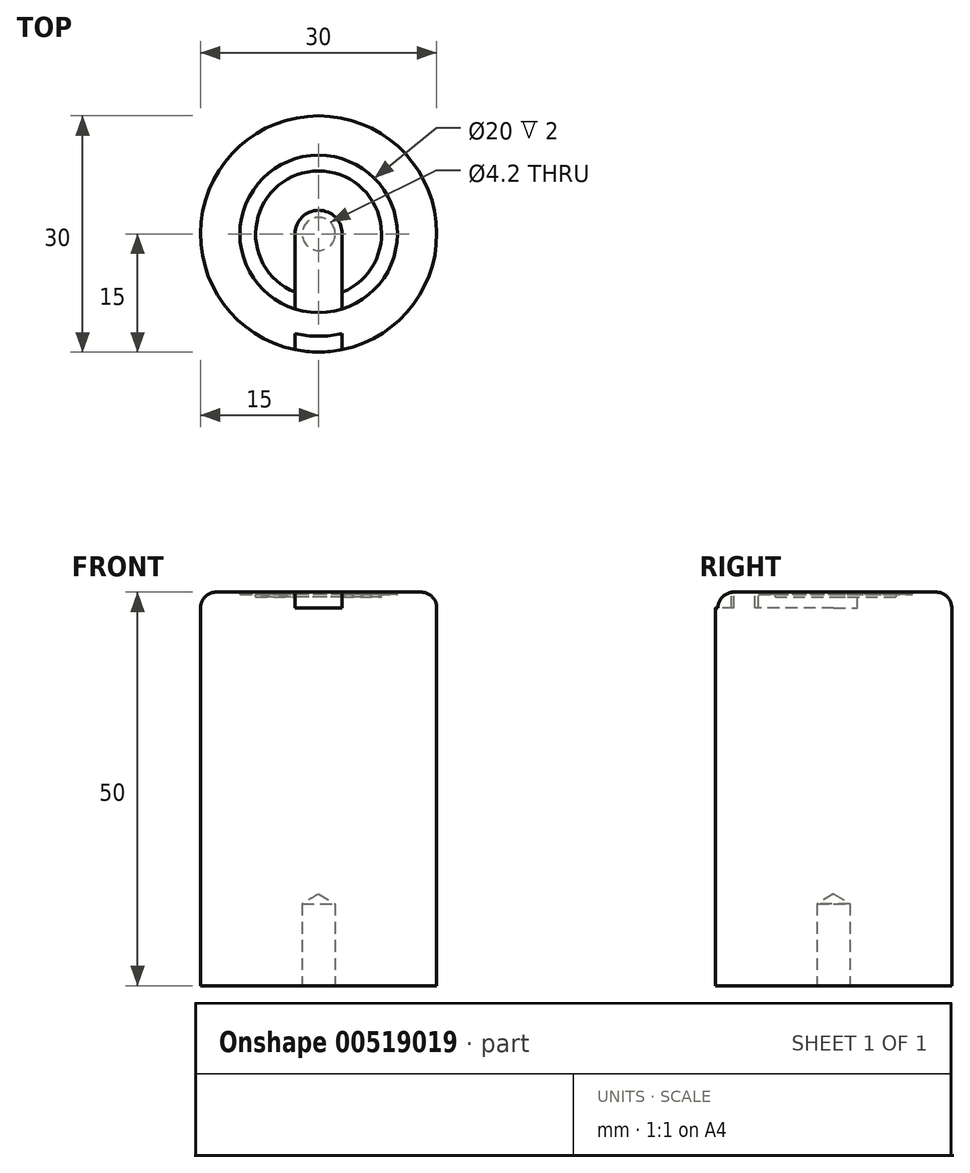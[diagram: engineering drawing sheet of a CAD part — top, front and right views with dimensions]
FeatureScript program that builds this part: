
annotation { "Feature Type Name" : "Feature", "Feature Type Description" : "" }
export const myFeature = defineFeature(function(context is Context, id is Id, definition is map)
    precondition{}
    {
        {
            var Q0;
            Q0=qCreatedBy(makeId("Top.planeOp"),FACE);
            var sketch = newSketch(context, id + "F0", { "sketchPlane" : qUnion([Q0])});
            skCircle(sketch, "E0", {"center": v(0, 0) * mm, "radius": 15 * mm});
            skSolve(sketch);
        }
        {
            var Q0;
            Q0 = qSketchRegion(id + "F0", true);
            extrude(context, id + "F1", {"entities" : qUnion([Q0]), "depth" : 50 * mm, "offsetDistance" : 25 * mm});
        }
        {
            var Q0;
            Q0=makeQuery(id+"F1.opExtrude","CAP_EDGE",EDGE,{"disambiguationData":[OSD([sQuery(id+"F0.wireOp",EDGE,"E0")])],"isStart":false});
            fillet(context, id + "F2", {"entities" : qUnion([Q0]), "radius" : 2 * mm, "tangentPropagation" : true, "allowEdgeOverflow" : false});
        }
        {
            var Q0;
            Q0=makeQuery(id+"F1.opExtrude","CAP_FACE",FACE,{"disambiguationData":[OSD([sQuery(id+"F0.wireOp",EDGE,"E0")])],"isStart":false});
            var sketch = newSketch(context, id + "F3", { "sketchPlane" : qUnion([Q0])});
            skCircle(sketch, "E1", {"center": v(0, 0) * mm, "radius": 10 * mm});
            skSolve(sketch);
        }
        {
            var Q0;
            Q0 = qSketchRegion(id + "F3", true);
            extrude(context, id + "F4", {"entities" : qUnion([Q0]), "operationType" : NewBodyOperationType.REMOVE, "oppositeDirection" : true, "depth" : 0.3 * mm, "offsetDistance" : 25 * mm});
        }
        {
            var Q0;
            Q0=makeQuery(id+"F1.opExtrude","CAP_FACE",FACE,{"disambiguationData":[OSD([sQuery(id+"F0.wireOp",EDGE,"E0")])],"isStart":false});
            var sketch = newSketch(context, id + "F5", { "sketchPlane" : qUnion([Q0])});
            skLineSegment(sketch, "E2.bottom", {"start": v(0, 3) * mm, "end": v(0, 3) * mm});
            skLineSegment(sketch, "E2.top", {"start": v(-3, -27) * mm, "end": v(3, -27) * mm});
            skLineSegment(sketch, "E2.left", {"start": v(-3, 0) * mm, "end": v(-3, -27) * mm});
            skLineSegment(sketch, "E2.right", {"start": v(3, 0) * mm, "end": v(3, -27) * mm});
            skPoint(sketch, "E3.visualSharp", {"position": v(3, 3) * mm});
            skArc(sketch, "E3.filletArc", {"start": v(3, 0) * mm, "mid": v(2.12, 2.12) * mm, "end": v(0, 3) * mm});
            skPoint(sketch, "E4.visualSharp", {"position": v(-3, 3) * mm});
            skArc(sketch, "E4.filletArc", {"start": v(0, 3) * mm, "mid": v(-2.12, 2.12) * mm, "end": v(-3, 0) * mm});
            skSolve(sketch);
        }
        {
            var Q0;
            {var subQ1=sQuery(id+"F5.wireOp",EDGE,"E3.filletArc");Q0=makeQuery(id+"F5.imprint","IMPRINT",FACE,{"disambiguationData":[TD([[makeQuery(id+"F5.imprint","IMPRINT",EDGE,{"derivedFrom":subQ1}),1.0]])]});}
            var Q1;
            {var subQ0=sQuery(id+"F5.wireOp",EDGE,"E2.left");var subQ4=makeQuery(id+"F4.boolean.opBoolean","COPY",EDGE,{"derivedFrom":makeQuery(id+"F4.opExtrude","CAP_EDGE",EDGE,{"disambiguationData":[OSD([sQuery(id+"F3.wireOp",EDGE,"E1")])],"isStart":true})});var subQ5=makeQuery(id+"F5.imprint","INTERSECT",VERTEX,{"derivedFrom":[subQ4,subQ0]});Q1=makeQuery(id+"F5.imprint","IMPRINT",FACE,{"disambiguationData":[TD([[makeQuery(id+"F5.imprint","IMPRINT",EDGE,{"disambiguationData":[TD([[subQ5,-1.0]])],"derivedFrom":subQ4}),-1.0]])]});}
            var Q2;
            {var subQ0=sQuery(id+"F5.wireOp",EDGE,"E2.top");Q2=makeQuery(id+"F5.imprint","IMPRINT",FACE,{"disambiguationData":[TD([[makeQuery(id+"F5.imprint","IMPRINT",EDGE,{"derivedFrom":subQ0}),1.0]])]});}
            extrude(context, id + "F6", {"entities" : qUnion([Q0, Q1, Q2]), "operationType" : NewBodyOperationType.REMOVE, "oppositeDirection" : true, "depth" : 2 * mm, "offsetDistance" : 25 * mm});
        }
        {
            var Q0;
            Q0=makeQuery(id+"F1.opExtrude","CAP_FACE",FACE,{"disambiguationData":[OSD([sQuery(id+"F0.wireOp",EDGE,"E0")])],"isStart":true});
            var sketch = newSketch(context, id + "F7", { "sketchPlane" : qUnion([Q0])});
            skCircle(sketch, "E5", {"center": v(0, 0) * mm, "radius": 3.5 * mm});
            skSolve(sketch);
        }
        {
            var Q0;
            Q0=sQuery(id+"F7.wireOp",VERTEX,"E5.center");
            var Q1;
            Q1=makeQuery(id+"F1.opExtrude","SWEPT_BODY",BODY,{"disambiguationData":[OSD([sQuery(id+"F0.wireOp",EDGE,"E0")])]});
            hole(context, id + "F8", {"style" : HoleStyle.SIMPLE, "endStyle" : HoleEndStyle.BLIND, "standardTappedOrClearance" : lookupTablePath({ "standard" : "ISO", "engagement" : "75%", "pitch" : "0.8 mm", "size" : "M5", "type" : "Tapped" }), "standardBlindInLast" : lookupTablePath({ "standard" : "ISO", "engagement" : "75%", "pitch" : "0.8 mm", "size" : "M5", "type" : "Tapped" }), "holeDiameter" : 4.2 * mm, "showTappedDepth" : true, "holeDepth" : 10.4 * mm, "isTappedThrough" : true, "tappedDepth" : 8 * mm, "tapClearance" : 3, "locations" : qUnion([Q0]), "scope" : qUnion([Q1]), "majorDiameter" : 5 * mm});
        }
        {
            var Q0;
            Q0=makeQuery(id+"F4.boolean.opBoolean","COPY",FACE,{"derivedFrom":makeQuery(id+"F4.opExtrude","CAP_FACE",FACE,{"disambiguationData":[OSD([sQuery(id+"F3.wireOp",EDGE,"E1")])],"isStart":false})});
            var sketch = newSketch(context, id + "F9", { "sketchPlane" : qUnion([Q0])});
            skCircle(sketch, "E6", {"center": v(0, 0) * mm, "radius": 8 * mm});
            skSolve(sketch);
        }
        {
            var Q0;
            Q0 = qSketchRegion(id + "F9", true);
            extrude(context, id + "F10", {"entities" : qUnion([Q0]), "operationType" : NewBodyOperationType.REMOVE, "oppositeDirection" : true, "depth" : 0.3 * mm, "offsetDistance" : 25 * mm});
        }
    });
